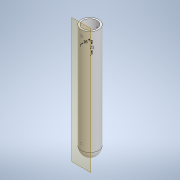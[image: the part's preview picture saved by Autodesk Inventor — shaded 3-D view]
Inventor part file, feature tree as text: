
AUTODESK INVENTOR PART (.ipt)
format: ipt  version: 2022.3 (Build 263350000, 350)  size: 246,784 bytes
history: native  units: mm
features: extrude x11, sketch x10, hole x2, projected_geometry x2, revolve x1, plane x1, mirror x1, sweep x1, fillet x1
ambient origin geometry x8: Origin, YZ Plane, XZ Plane, XY Plane, X Axis, Y Axis, Z Axis, Center Point
bodies: Solid1 (feature_tree)
feature tree (30):
  extrude  "Extrusion1"  Depth=3.0mm
  revolve  "Revolution1"  [1 undecoded]
  sketch  "Sketch3"  dims[d2=180.0mm d3=0.0mm d4=15.0mm]
  extrude  "Extrusion2"  TaperAngle=90.0deg  [1 undecoded]
  extrude  "Extrusion3"  Depth=10.0mm
  extrude  "Extrusion4"  Depth=200.0mm TaperAngle=0.0deg
  extrude  "Extrusion5"  Depth=10.0mm TaperAngle=0.0deg
  sketch  "Sketch4"  dims[d5=15.0mm d6=90.0deg]
  extrude  "Extrusion6"  Depth=30.0mm TaperAngle=0.0deg
  extrude  "Extrusion7"  Depth=0.1mm
  plane  "Work Plane1"
  hole  "Hole1"  [1 undecoded]
  mirror  "Mirror1"
  extrude  "Extrusion8"  Depth=1.0mm TaperAngle=0.0deg
  sketch  "Sketch7"  dims[d12=200.0mm d13=0.0mm d14=10.0mm d15=0.0mm]
  extrude  "Extrusion9"  Depth=1.0mm
  extrude  "Extrusion10"  Depth=6.0mm
  hole  "Hole2"  [1 undecoded]
  sweep  "Sweep1"
  extrude  "Extrusion11"  Depth=1.0mm
  fillet  "Fillet1"  Radius=15.0mm
  sketch  "Sketch1"  dims[d0=30.0mm d1=3.0mm]
  sketch  "Sketch5"  dims[d7=10.0mm d8=3.0mm]
  sketch  "Sketch6"  dims[d9=5.0mm d10=200.0mm d11=0.0mm]
  projected_geometry  "Projected Loop1"
  sketch  "Sketch8"  dims[d16=5.075mm d17=0.0mm d18=30.0mm d19=0.0mm]
  sketch  "Sketch10"  dims[d20=25.0mm d21=0.0mm d22=0.1mm]
  sketch  "Sketch11"  dims[d23=15.0mm d24=10.0mm]
  sketch  "Sketch12"  dims[d25=2.2mm d26=6.0mm d27=4.0mm d28=2.0mm d29=90.0deg d30=5.0mm d31=0.0mm d32=155.0mm d33=0.0mm d34=22.0mm d35=6.0mm d36=51.0mm d37=0.0mm d38=30.0mm d39=0.0mm d40=7.5mm d41=15.0mm d42=0.0mm d43=2.2mm d44=6.0mm d45=3.1mm d46=4.1mm d47=90.0deg d48=0.9mm d49=0.0mm d52=15.0mm d53=1.0mm d54=12.0mm d55=20.0mm d56=15.0mm d57=20.0mm d58=2.0mm d59=0.0mm d60=0.0mm d61=2.0mm d62=2.0mm d63=0.0mm d64=1.0mm d50=0.75mm d51=20.594885mm]
  projected_geometry  "Projected Loop2"
note: 4 required parameter values undecoded (feature->parameter linkage not recoverable at this tier; creation-order binding heuristic only, values carry confidence <= 0.55)